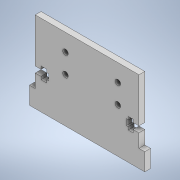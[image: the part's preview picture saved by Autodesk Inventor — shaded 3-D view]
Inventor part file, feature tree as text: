
AUTODESK INVENTOR PART (.ipt)
format: ipt  version: 2022 (Build 260153000, 153)  size: 175,104 bytes
history: native  units: mm
features: reference x4, other x2, extrude x1, sketch x1
ambient origin geometry x8: Origin, YZ Plane, XZ Plane, XY Plane, X Axis, Y Axis, Z Axis, Center Point
bodies: Solid1 (feature_tree)
feature tree (8):
  extrude  "Extrusion1"  Depth=9.0mm
  sketch  "Sketch1"  dims[d9=7.0mm d10=2.5mm d27=3.0mm d28=0.0mm d54=3.1mm d70=3.1mm d74=1.5mm d83=3.0mm d85=3.1mm d87=3.0mm d100=9.0mm d102=3.1mm d103=0.0mm d104=0.0mm d105=53.5mm d108=3.0mm d109=9.0mm d110=9.0mm d111=0.0mm d112=3.0mm d113=3.0mm d114=2.5mm d115=1.0mm d116=1.0mm d117=1.5mm d121=8.5mm d122=1.55mm d123=6.95mm d124=6.95mm d125=1.0mm d126=1.0mm d127=3.0mm d128=3.0mm d129=1.5mm d130=1.5mm d131=0.0mm d132=1.5mm d133=1.5mm d134=1.5mm d136=27.0mm d137=9.95mm]
  reference  "Reference5"
  reference  "Reference6"
  reference  "Reference7"
  reference  "Reference8"
  other  "EnsambleCuerpo.iam"
  other  "Muñeca2:1"
